# Revit family: IS_Ceravito_B0411_BIM_DE
name_source: partatom
category: Plumbing Fixtures
revit_build: Autodesk Revit MEP 2016 (Build: 20161004_0715(x64)
units: mm (PartAtom-declared; Revit-internal decimal feet)

## family parameters
Always vertical = No
Cut with Voids When Loaded = No
OmniClass Number = 23.45.55.17
OmniClass Title = Mixing Faucets
Part Type = Normal
Room Calculation Point = No
Round Connector Dimension = Use Diameter
Shared = No
Work Plane-Based = No

## types (1)
- B0411AA - CERAVITO exposed shower single lever mixer
    Accessories = www.idealstandard.de\ersatzteile
    AssetType = Fixed
    BIMObjectName = ISI_IdealStandard_ShowerManualWaterSupplySets_Ceravito_B0411AA
    BIMobject category = Taps & Mixers
    BOSUseNativeGeometries = 1
    BarCode = 3800861039518
    Brand = Ideal Standard
    Brand url = http://www.idealstandard.de
    CodePerformance = EN 817, DIN 4109, Gruppe 1
    Color = Chrome
    ConnectionType = Plumbing
    Cost = 0 $
    CurrencyUnit = €
    CurrentRevision = 1
    Date of publishing = 20/12/2017
    Description = IS Brausearmatur AP CERAVITO, Ausld.173mm, Chrom
    DurationUnit = Year
    EAN code = https://3800861039518
    Edition number = 1
    ExpectedLife = 25
    Features = IS Brausearmatur AP CERAVITO, Ausld.173mm, Chrom
    Finish = Chrome
    IFC Classification = Sanitary Terminal
    IfcExportAs = IfcSanitaryTerminalType
    InletConnectionSize = 0 mm  [stored 0 ft]
    Installation instructions = http://www.idealstandard.de
    InstallationInstructions = www.idealstandard.de\produkte
    MainColor = Chrome
    MaintenanceInformation = www.idealstandard.de\produkte
    Manufacturer name = Ideal Standard
    ManufacturerURL = http://www.idealstandard.de
    Material = Brass
    Material main = Brass
    Model = B0411AA
    ModelNumber = B0411AA
    ModelReference = IS Brausearmatur AP CERAVITO, Ausld.173mm, Chrom
    NBS Reference Code = 35-06-82
    NBS Reference Description = Shower Mixers
    Name = ShowerManualWaterSupplySets_Ceravito_B0411AA
    NettWeight = 1.48 Kg
    Nominal height = 0
    Nominal width = 0
    NominalDepth = 129 mm  [stored 0.423228 ft]
    NominalHeight = 113 mm
    NominalLength = 129 mm  [stored 0.423228 ft]
    NominalWidth = 220 mm
    OmniClass Code = 23-31 11 00
    OmniClass Description = Faucets
    Product Guid = 17309409-52d6-4b7d-bc77-6635d26b9bd7
    Product SKU = B0411
    Product data url = https://bimobject.com
    Product family = Sanitary
    Product group = Shower Mixer
    Product name = CERAVITO exposed shower single lever mixer
    Product url = http://www.idealstandard.de
    ProductInformation = www.idealstandard.de/produkte
    QR code = http://bimobject.com
    Shape = Sculptured
    Size = 113 x 129 x 220mm
    Space = Internal
    SpareParts = www.idealstandard.de/ersatzteile
    Technical description = http://www.idealstandard.de
    TestPressure = 10 Bar
    URL = http://www.idealstandard.de
    Uniclass 1.4 Code = L8212
    Uniclass 1.4 Description = Fittings
    Uniclass 2.0 Code = PR-35-06-82
    Uniclass 2.0 Description = Shower Mixers
    Uniclass 2015 Code = Pr_40_20_87_78
    Uniclass 2015 Name = Shower manual water supply sets
    Uniclass2015Code = Pr_40_20_87_78
    Uniclass2015Title = Shower manual water supply sets
    Uniclass2015Version = Products v1.1
    Version = 1
    VolumeUnits = Litres
    Weight Net (Kg) = 1.48

note: [stored X ft] marks values corroborated as IEEE doubles in the binary element streams (Revit-internal decimal feet)

## geometry (parser evidence)
native form markers: Blend x4
no freeform markers — native parametric forms only
